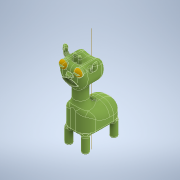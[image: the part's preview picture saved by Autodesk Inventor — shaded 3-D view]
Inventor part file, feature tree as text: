
AUTODESK INVENTOR PART (.ipt)
format: ipt  version: 2022 (Build 260153000, 153)  size: 4,324,352 bytes
history: native  units: mm
features: fillet x44, extrude x18, sketch x12, plane x5, mirror x3
ambient origin geometry x8: Origin, YZ Plane, XZ Plane, XY Plane, X Axis, Y Axis, Z Axis, Center Point
bodies: Solid1 (feature_tree), Solid2 (feature_tree)
feature tree (82):
  extrude  "Extrusion1"  Depth=30.0mm
  extrude  "Extrusion2"  Depth=15.0mm
  extrude  "Extrusion3"  Depth=2.0mm TaperAngle=0.0deg
  plane  "Work Plane1"
  plane  "Work Plane2"
  extrude  "Extrusion4"  Depth=9.0mm
  fillet  "Fillet1"  Radius=20.0mm
  fillet  "Fillet2"  Radius=48.0mm
  extrude  "Extrusion5"  Depth=8.0mm
  extrude  "Extrusion6"  Depth=6.0mm
  fillet  "Fillet4"  Radius=5.7mm
  plane  "Work Plane4"
  extrude  "Extrusion11"  Depth=6.0mm
  extrude  "Extrusion12"  Depth=0.1mm
  fillet  "Fillet5"  Radius=0.1mm
  extrude  "Extrusion13"  Depth=3.0mm
  fillet  "Fillet6"  Radius=3.0mm
  fillet  "Fillet7"  Radius=3.0mm
  plane  "Work Plane5"
  extrude  "Extrusion14"  TaperAngle=0.0deg  [1 undecoded]
  plane  "Work Plane6"
  extrude  "Extrusion15"  Depth=3.0mm
  fillet  "Fillet8"  Radius=0.5mm
  fillet  "Fillet9"  Radius=2.1mm
  fillet  "Fillet10"  Radius=0.1mm
  fillet  "Fillet11"  Radius=2.0mm
  fillet  "Fillet12"  Radius=3.0mm
  fillet  "Fillet13"  Radius=3.0mm
  mirror  "Mirror1"
  fillet  "Fillet14"  Radius=3.0mm
  extrude  "Extrusion18"  Depth=3.0mm
  fillet  "Fillet20"  Radius=1.0mm
  fillet  "Fillet21"  Radius=0.58mm
  fillet  "Fillet22"  Radius=0.58mm
  fillet  "Fillet23"  Radius=0.58mm
  fillet  "Fillet25"  Radius=0.5mm
  fillet  "Fillet26"  Radius=0.2mm
  extrude  "Extrusion20"  Depth=3.0mm
  fillet  "Fillet27"  Radius=0.3mm
  fillet  "Fillet29"  Radius=0.1mm
  fillet  "Fillet32"  Radius=0.1mm
  extrude  "Extrusion22"  Depth=3.0mm TaperAngle=0.0deg
  fillet  "Fillet33"  Radius=0.1mm
  fillet  "Fillet34"  Radius=0.1mm
  extrude  "Extrusion23"  Depth=3.0mm
  mirror  "Mirror3"
  fillet  "Fillet35"  Radius=1.0mm
  fillet  "Fillet36"  Radius=2.0mm
  fillet  "Fillet37"  Radius=3.0mm
  fillet  "Fillet38"  Radius=2.0mm
  fillet  "Fillet39"  Radius=4.0mm
  fillet  "Fillet40"  Radius=0.1mm
  fillet  "Fillet41"  Radius=0.5mm
  fillet  "Fillet42"  Radius=11.0mm
  fillet  "Fillet43"  Radius=5.0mm
  fillet  "Fillet44"  Radius=5.0mm
  extrude  "Extrusion24"  Depth=3.0mm
  mirror  "Mirror4"
  fillet  "Fillet45"  Radius=5.0mm
  fillet  "Fillet46"  Radius=12.0mm
  extrude  "Extrusion25"  Depth=3.0mm
  fillet  "Fillet47"  Radius=1.0mm
  fillet  "Fillet48"  Radius=10.25mm
  extrude  "Extrusion26"  Depth=3.0mm
  fillet  "Fillet49"  Radius=1.5mm
  fillet  "Fillet50"  Radius=1.0mm
  fillet  "Fillet51"  Radius=1.0mm
  fillet  "Fillet52"  Radius=4.0mm
  fillet  "Fillet53"  Radius=32.5mm
  fillet  "Fillet54"  Radius=0.2mm
  sketch  "Sketch1"  dims[d1=20.0mm d3=30.0mm]
  sketch  "Sketch2"  dims[d4=10.0mm d5=15.0mm]
  sketch  "Sketch3"  dims[d6=12.0mm d7=0.0mm d8=2.0mm d9=0.0mm]
  sketch  "Sketch6"  dims[d10=10.0mm d11=9.0mm d12=20.0mm d13=0.0mm d21=48.0mm d22=35.0mm]
  sketch  "Sketch13"  dims[d38=7.0mm d39=0.0mm d40=8.0mm]
  sketch  "Sketch22"  dims[d41=4.0mm d43=6.0mm d44=5.7mm]
  sketch  "Sketch24"  dims[d45=6.0mm d46=6.0mm]
  sketch  "Sketch26"  dims[d47=2.0mm d48=0.0mm d49=0.1mm d50=0.1mm]
  sketch  "Sketch27"  dims[d51=3.5mm d52=0.0mm d53=2.5mm d72=3.0mm d73=3.0mm]
  sketch  "Sketch28"  dims[d74=3.0mm d75=-2.268928mm d76=0.0mm]
  sketch  "Sketch29"  dims[d77=0.0mm d78=2.1mm d79=1.919862mm d80=0.5mm d81=2.1mm d82=-3.490659mm d83=0.1mm d84=2.0mm d85=3.0mm d86=3.0mm d87=-1.745329mm d88=3.0mm d89=0.0mm]
  sketch  "Sketch30"  dims[d90=2.0mm d91=1.0mm d92=1.0mm d93=0.58mm d94=0.58mm d95=0.58mm d96=0.5mm d106=0.2mm d107=0.0mm d111=0.3mm d112=0.3mm d113=0.1mm d114=0.1mm d115=0.6mm d116=0.0mm d117=0.1mm d118=0.1mm d119=0.1mm d120=0.1mm d124=1.0mm d125=2.0mm d126=3.0mm d127=3.0mm d128=2.0mm d129=4.0mm d130=-5.235988mm d134=0.1mm d136=0.5mm d139=11.0mm d140=0.0mm d141=8.0mm d142=5.0mm d143=5.0mm d144=5.0mm d145=5.0mm d146=12.0mm d147=0.0mm d148=2.0mm d149=1.0mm d150=10.25mm d151=9.0mm d152=1.2mm d153=1.5mm d154=0.0mm d155=1.0mm d156=1.0mm d157=4.0mm d159=32.5mm d160=0.2mm d161=0.2mm d162=0.2mm d163=0.2mm d164=0.05mm d165=0.1mm d166=0.1mm d167=1.0mm d168=0.0mm d169=2.0mm d170=2.0mm d171=4.0mm d172=0.0mm d173=2.0mm d174=0.2mm d175=2.0mm d176=0.0mm d177=1.0mm d178=1.0mm d179=0.5mm d180=0.3mm d181=0.11mm d182=3.0mm d63=0.0mm d64=0.0mm d65=0.0mm d66=0.0mm]
note: 1 required parameter value undecoded (feature->parameter linkage not recoverable at this tier; creation-order binding heuristic only, values carry confidence <= 0.55)
